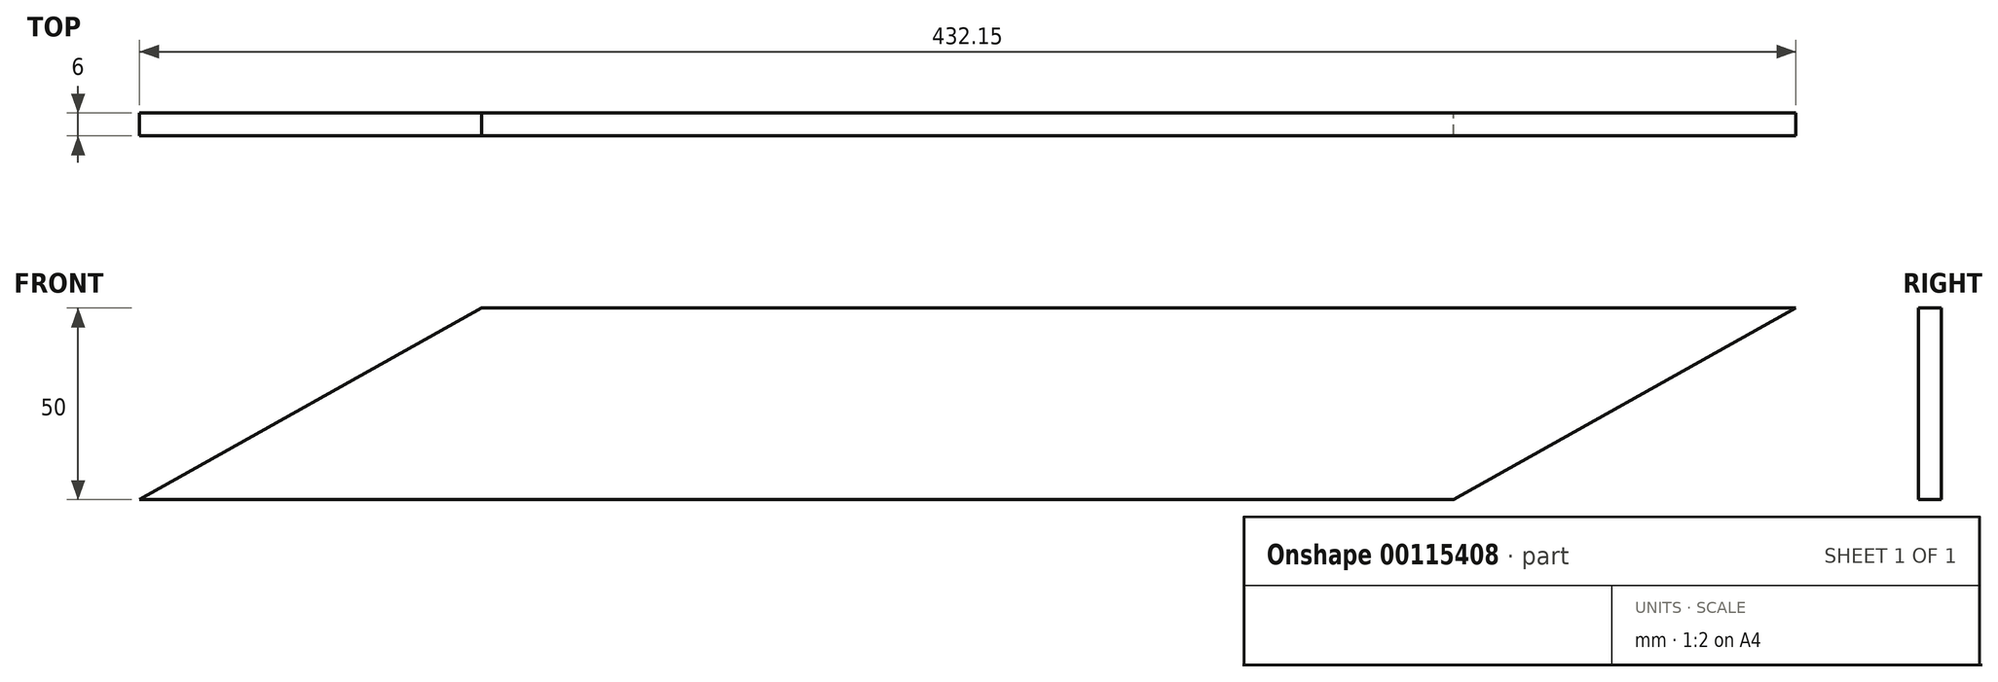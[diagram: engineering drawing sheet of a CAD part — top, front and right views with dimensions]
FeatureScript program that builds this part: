
annotation { "Feature Type Name" : "Feature", "Feature Type Description" : "" }
export const myFeature = defineFeature(function(context is Context, id is Id, definition is map)
    precondition{}
    {
        {
            var Q0;
            Q0=qCreatedBy(makeId("Front.planeOp"),FACE);
            var sketch = newSketch(context, id + "F0", { "sketchPlane" : qUnion([Q0])});
            skLineSegment(sketch, "E0.bottom", {"start": v(-127.1, 24.85) * mm, "end": v(126.48, 24.85) * mm});
            skLineSegment(sketch, "E0.top", {"start": v(-127.1, -25.15) * mm, "end": v(126.48, -25.15) * mm});
            skLineSegment(sketch, "E0.left", {"start": v(-127.1, 24.85) * mm, "end": v(-127.1, -25.15) * mm});
            skLineSegment(sketch, "E0.right", {"start": v(126.48, 24.85) * mm, "end": v(126.48, -25.15) * mm});
            skLineSegment(sketch, "E1", {"start": v(126.48, -25.15) * mm, "end": v(215.77, 24.85) * mm});
            skLineSegment(sketch, "E2", {"start": v(215.77, 24.85) * mm, "end": v(126.48, 24.85) * mm});
            skLineSegment(sketch, "E3", {"start": v(-127.1, 24.85) * mm, "end": v(-216.38, -25.15) * mm});
            skLineSegment(sketch, "E4", {"start": v(-216.38, -25.15) * mm, "end": v(-127.1, -25.15) * mm});
            skSolve(sketch);
        }
        {
            var Q0;
            Q0 = qSketchRegion(id + "F0", true);
            extrude(context, id + "F1", {"entities" : qUnion([Q0]), "depth" : 6 * mm});
        }
    });
